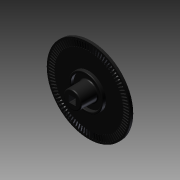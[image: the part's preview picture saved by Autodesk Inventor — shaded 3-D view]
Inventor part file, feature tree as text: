
AUTODESK INVENTOR PART (.ipt)
format: ipt  version: 2013 (Build 170138000, 138)  size: 519,680 bytes
history: native  units: in
note: dims shown in document units (in); Inventor stores cm internally (conversion verified against a paired STEP export)
features: extrude x6, sketch x6, fillet x2, mirror x1, pattern_circular x1, other x1
ambient origin geometry x8: Origin, YZ Plane, XZ Plane, XY Plane, X Axis, Y Axis, Z Axis, Center Point
bodies: Solid1 (feature_tree)
feature tree (17):
  extrude  "Extrusion1"  Depth=0.049in TaperAngle=0.0deg
  extrude  "Extrusion2"  Depth=0.31in
  fillet  "Fillet1"  Radius=0.02in
  extrude  "Extrusion3"  Depth=0.041in
  fillet  "Fillet2"  Radius=0.059in
  mirror  "Mirror1"
  extrude  "Extrusion4"  Depth=0.059in TaperAngle=0.0deg
  extrude  "Extrusion5"  Depth=35.4331in TaperAngle=360.0deg
  pattern_circular  "Circular Pattern1"  [2 undecoded]
  sketch  "Sketch1"  dims[d0=1.575in d1=0.049in d2=0.0in]
  sketch  "Sketch2"  dims[d3=0.3401in d4=0.31in d5=-0.0034in d6=0.02in]
  sketch  "Sketch3"  dims[d7=0.5688in d8=0.041in d9=0.059in d10=-0.0069in]
  sketch  "Sketch4"  dims[d11=0.012in d12=0.059in d13=0.0in]
  sketch  "Sketch5"  dims[d14=0.059in d15=0.0in d16=35.4331in d17=360.0deg]
  sketch  "Sketch6"  dims[d19=0.059in d20=0.0in d21=0.0in d22=0.0in]
  other  "Srf1"
  extrude  "ExtrusionSrf1"  TaperAngle=0.0deg  [1 undecoded]
note: 3 required parameter values undecoded (feature->parameter linkage not recoverable at this tier; creation-order binding heuristic only, values carry confidence <= 0.55)
